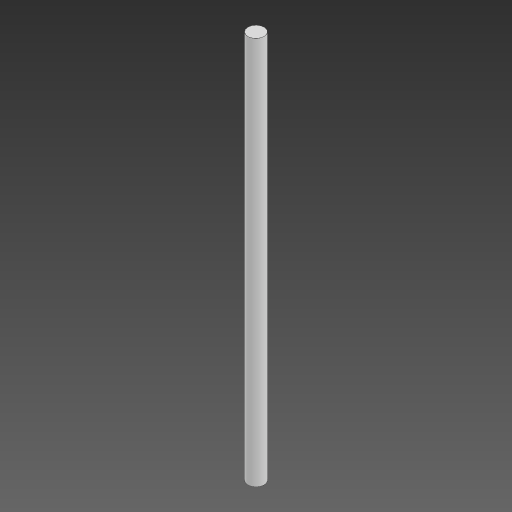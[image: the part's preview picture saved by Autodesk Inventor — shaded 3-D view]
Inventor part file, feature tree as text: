
AUTODESK INVENTOR PART (.ipt)
format: ipt  version: 2024 (Build 280153000, 153)  size: 74,240 bytes
history: native  units: in
note: dims shown in document units (in); Inventor stores cm internally (conversion verified against a paired STEP export)
features: extrude x1, sketch x1
ambient origin geometry x8: Origin, YZ Plane, XZ Plane, XY Plane, X Axis, Y Axis, Z Axis, Center Point
bodies: Solid1 (feature_tree)
feature tree (2):
  extrude  "Extrusion1"  Depth=6.0in TaperAngle=0.0deg
  sketch  "Sketch1"  dims[d0=0.25in d1=6.0in d2=0.0in]
